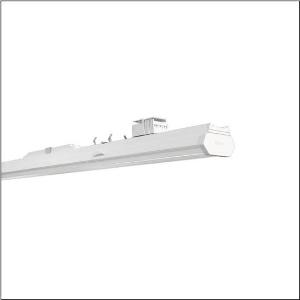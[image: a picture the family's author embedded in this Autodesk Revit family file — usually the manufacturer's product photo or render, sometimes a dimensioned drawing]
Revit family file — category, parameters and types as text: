
# Revit family: licross_11_protected_ho_51td1bcn4d5m
name_source: partatom
category: Lighting Fixtures
units: mm (PartAtom-declared; Revit-internal decimal feet)

## family parameters
Cut with Voids When Loaded = No
Host = Face
Light Source = No
Part Type = Normal
Room Calculation Point = No
Round Connector Dimension = Use Diameter
Shared = No

## types (1)
- --- (1 x LED, 13520 lm, 77.6 W, 4000K)
    Apparent Load = 78 VA
    CIE Flux Codes = 54 82 95 97 100
    Color Rendering = 80
    Color Temperature = 4000K
    Default Elevation = 1800 mm
    Description = Licross 11 Protected HO, luminaire insert, of sheet steel, galvanised, coil coated, white, length: 1.500mm, width: 90mm, height: 101mm, LED rated luminous flux: 13.520lm, light colour: 840, SDCM (Standard Deviation of Colour Matching)MacAdam ≤ 2 SDCM (initial), control gear: ON/OFF Multilumen, CLOi, with plug, 3-pole, with phase selection, mains connection: 220..240V, AC, 50/60Hz, start of lifetime: 78W, end of service life: 87W, internal wiring halogen-free, primary optical cover: cover, of PMMA, light emission: direct distribution, primary light characteristic: symmetric, protection rating (complete): IP54, insulation class (complete): insulation class I (protective earthing), certification: CE, ENEC, VDE, UKCA, protection symbol: D if used in an environment with non-conductive dust loads with corresponding accessories, impact resistance: IK06, permissible ambient temperature for indoor applications: -35..+35°C, corresponds to IFS (International Featured Standards) requirements for safety and quality in the food industry, reducing of maximum allowable ambient temperature of 5°C with ceiling mounting, LABS conformity tested according to VDMA 24364:2018-05, The light source and the operating device comply with the requirements of the Ecodesign Regulation (EU) 2019/2020 and are replaceable in accordance with this regulation, packaging unit: 1 piece
    Height = 92 mm
    Lamp = 1 x LED
    Lamp Light Flux = 13520 lm
    Lamp Power = 77.6 W
    Lamp count = 1
    Length = 1500 mm
    Luminous efficacy = 174 lm/W
    Manufacturer = Siteco
    ModVariant = No
    Model = 51TD1BCN4D5M
    Mounting Place = Ceiling
    Mounting Type = Pendant
    Number of Poles = 1
    OnlyDefault = Yes
    Power Factor = 1
    Product Name = Licross 11 Protected HO
    Product group = luminaire insert | ceiling pendant
    ProductGroupID = 901
    Protection Class = Protection class I
    Protection Degree = IP 54
    RLX_Detail_Level = 1
    RLX_Emergency_Light_Flux = 0 lm
    RLX_Emergency_Type = 0
    RLX_Emergency_Type_DB = No
    RlxData = <blob elided: 22361 chars, md5=629544da>
    Socket = socket
    Standby Power = 0 W
    System Light Flux = 13520 lm
    System Power = 78 W
    Type Comments = factory setting: luminous flux: 100 % | (A | C | E) | 181 mA
    Type Image = l_1256145.jpg
    URL = http://relux.com
    VarID = @adj_000983
    Voltage = 0 V
    Weight = 0.00 kg
    Width = 88 mm

## geometry (parser evidence)
native form markers: Blend x4, Sweep x12
no freeform markers — native parametric forms only
